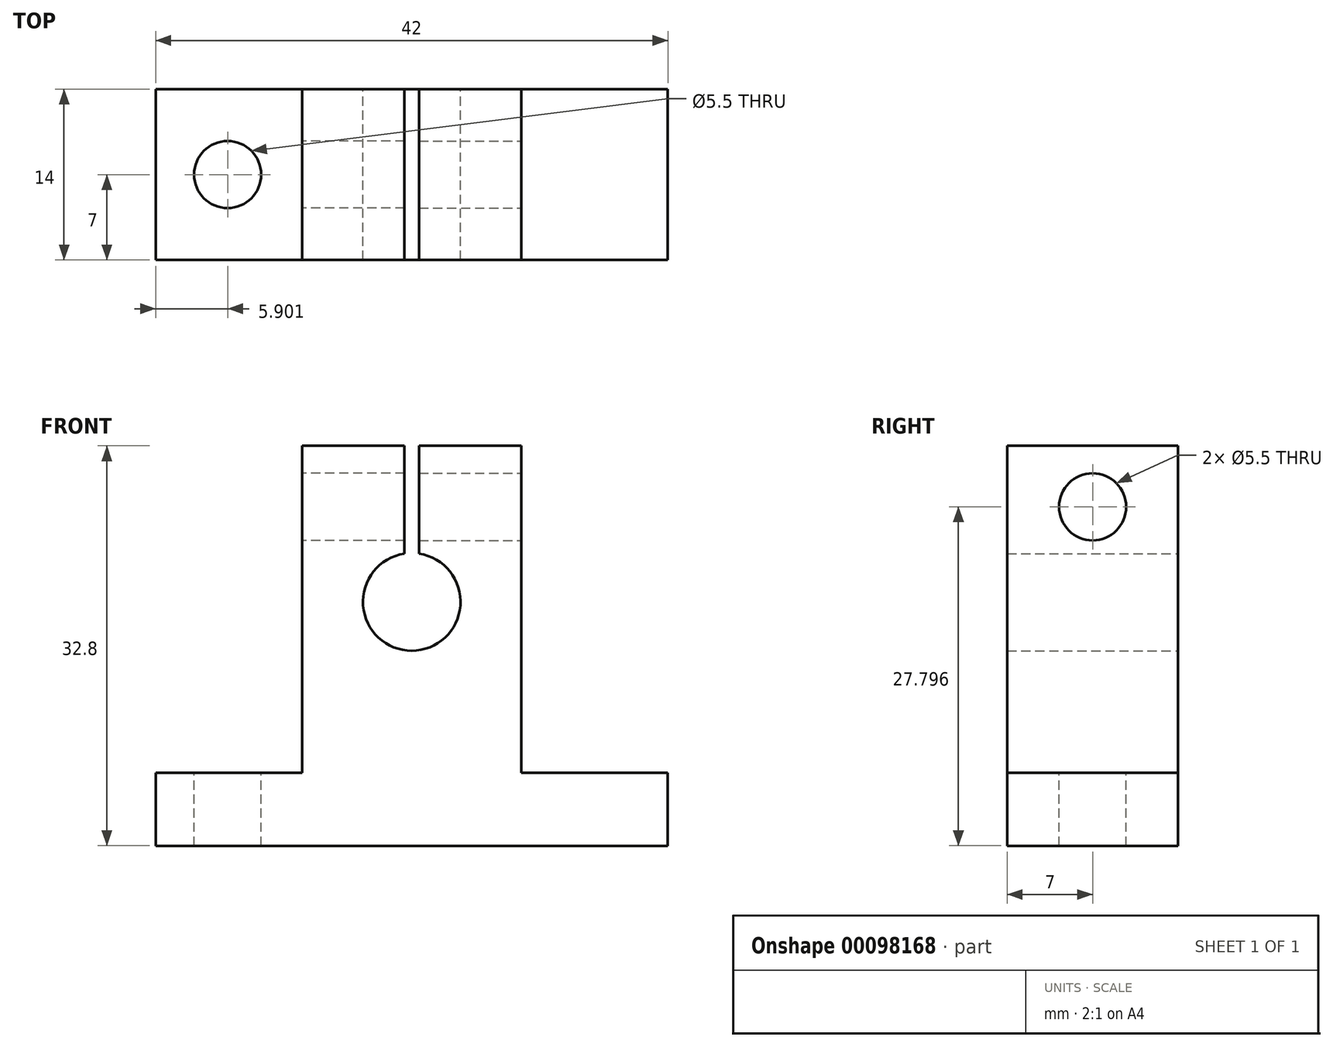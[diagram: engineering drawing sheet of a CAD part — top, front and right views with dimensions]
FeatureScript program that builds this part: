
annotation { "Feature Type Name" : "Feature", "Feature Type Description" : "" }
export const myFeature = defineFeature(function(context is Context, id is Id, definition is map)
    precondition{}
    {
        {
            var Q0;
            Q0=qCreatedBy(makeId("Front.planeOp"),FACE);
            var sketch = newSketch(context, id + "F0", { "sketchPlane" : qUnion([Q0])});
            skLineSegment(sketch, "E0", {"start": v(-45.5, 17.68) * mm, "end": v(-66.5, 17.68) * mm});
            skLineSegment(sketch, "E1", {"start": v(-66.5, 17.68) * mm, "end": v(-66.5, 23.68) * mm});
            skLineSegment(sketch, "E2", {"start": v(-66.5, 23.68) * mm, "end": v(-54.5, 23.68) * mm});
            skLineSegment(sketch, "E3", {"start": v(-54.5, 23.68) * mm, "end": v(-54.5, 50.48) * mm});
            skLineSegment(sketch, "E4", {"start": v(-45.5, 80.87) * mm, "end": v(-45.5, 4.96) * mm, "construction": true});
            skArc(sketch, "E5", {"start": v(-45.5, 33.68) * mm, "mid": v(-49.48, 37.38) * mm, "end": v(-46.1, 41.63) * mm});
            skLineSegment(sketch, "E6", {"start": v(-54.5, 50.48) * mm, "end": v(-46.1, 50.48) * mm});
            skLineSegment(sketch, "E7", {"start": v(-46.1, 50.48) * mm, "end": v(-46.1, 41.63) * mm});
            skLineSegment(sketch, "E8.MirrorCS", {"start": v(-45.5, 17.68) * mm, "end": v(-24.5, 17.68) * mm});
            skLineSegment(sketch, "E9.MirrorCS", {"start": v(-36.5, 23.68) * mm, "end": v(-36.5, 50.48) * mm});
            skLineSegment(sketch, "E10.MirrorCS", {"start": v(-24.5, 23.68) * mm, "end": v(-36.5, 23.68) * mm});
            skArc(sketch, "E11.MirrorCS", {"start": v(-45.5, 33.68) * mm, "mid": v(-41.5, 37.38) * mm, "end": v(-44.9, 41.63) * mm});
            skLineSegment(sketch, "E12.MirrorCS", {"start": v(-36.5, 50.48) * mm, "end": v(-44.9, 50.48) * mm});
            skLineSegment(sketch, "E13.MirrorCS", {"start": v(-24.5, 17.68) * mm, "end": v(-24.5, 23.68) * mm});
            skLineSegment(sketch, "E14.MirrorCS", {"start": v(-44.9, 50.48) * mm, "end": v(-44.9, 41.63) * mm});
            skSolve(sketch);
        }
        {
            var Q0;
            Q0 = qSketchRegion(id + "F0", true);
            extrude(context, id + "F1", {"entities" : qUnion([Q0]), "depth" : 14 * mm});
        }
        {
            var Q0;
            Q0=makeQuery(id+"F1.opExtrude","SWEPT_FACE",FACE,{"disambiguationData":[OSD([sQuery(id+"F0.wireOp",EDGE,"E2")])]});
            var sketch = newSketch(context, id + "F2", { "sketchPlane" : qUnion([Q0])});
            skCircle(sketch, "E15", {"center": v(-60.59, -7) * mm, "radius": 2.75 * mm});
            skLineSegment(sketch, "E16", {"start": v(-44.59, 1.94) * mm, "end": v(-44.59, -16.04) * mm, "construction": true});
            skCircle(sketch, "E17.MirrorC", {"center": v(-28.59, -7) * mm, "radius": 2.75 * mm});
            skSolve(sketch);
        }
        {
            var Q0;
            Q0=makeQuery(id+"F2.imprint","IMPRINT",FACE,{"disambiguationData":[TD([[makeQuery(id+"F2.imprint","IMPRINT",EDGE,{"derivedFrom":sQuery(id+"F2.wireOp",EDGE,"E15")}),1.0]])]});
            var Q1;
            Q1=makeQuery(id+"F2.imprint","IMPRINT",FACE,{"disambiguationData":[TD([[makeQuery(id+"F2.imprint","IMPRINT",EDGE,{"derivedFrom":sQuery(id+"F2.wireOp",EDGE,"E17.MirrorC")}),-1.0]])]});
            extrude(context, id + "F3", {"entities" : qUnion([Q0, Q1]), "operationType" : NewBodyOperationType.REMOVE, "oppositeDirection" : true, "depth" : 6 * mm});
        }
        {
            var Q0;
            Q0=makeQuery(id+"F1.opExtrude","SWEPT_FACE",FACE,{"disambiguationData":[OSD([sQuery(id+"F0.wireOp",EDGE,"E9.MirrorCS")])]});
            var sketch = newSketch(context, id + "F4", { "sketchPlane" : qUnion([Q0])});
            skCircle(sketch, "E18", {"center": v(-7, 45.48) * mm, "radius": 2.75 * mm});
            skSolve(sketch);
        }
        {
            var Q0;
            Q0=makeQuery(id+"F4.imprint","IMPRINT",FACE,{"disambiguationData":[TD([[makeQuery(id+"F4.imprint","IMPRINT",EDGE,{"derivedFrom":sQuery(id+"F4.wireOp",EDGE,"E18")}),1.0]])]});
            extrude(context, id + "F5", {"entities" : qUnion([Q0]), "operationType" : NewBodyOperationType.REMOVE, "oppositeDirection" : true, "depth" : 9 * mm});
        }
        {
            var Q0;
            Q0=makeQuery(id+"F1.opExtrude","SWEPT_FACE",FACE,{"disambiguationData":[OSD([sQuery(id+"F0.wireOp",EDGE,"E3")])]});
            var sketch = newSketch(context, id + "F6", { "sketchPlane" : qUnion([Q0])});
            skCircle(sketch, "E19", {"center": v(7, 45.48) * mm, "radius": 2.75 * mm});
            skSolve(sketch);
        }
        {
            var Q0;
            Q0=makeQuery(id+"F6.imprint","IMPRINT",FACE,{"disambiguationData":[TD([[makeQuery(id+"F6.imprint","IMPRINT",EDGE,{"derivedFrom":sQuery(id+"F6.wireOp",EDGE,"E19")}),1.0]])]});
            extrude(context, id + "F7", {"entities" : qUnion([Q0]), "operationType" : NewBodyOperationType.REMOVE, "oppositeDirection" : true, "depth" : 9 * mm});
        }
    });
